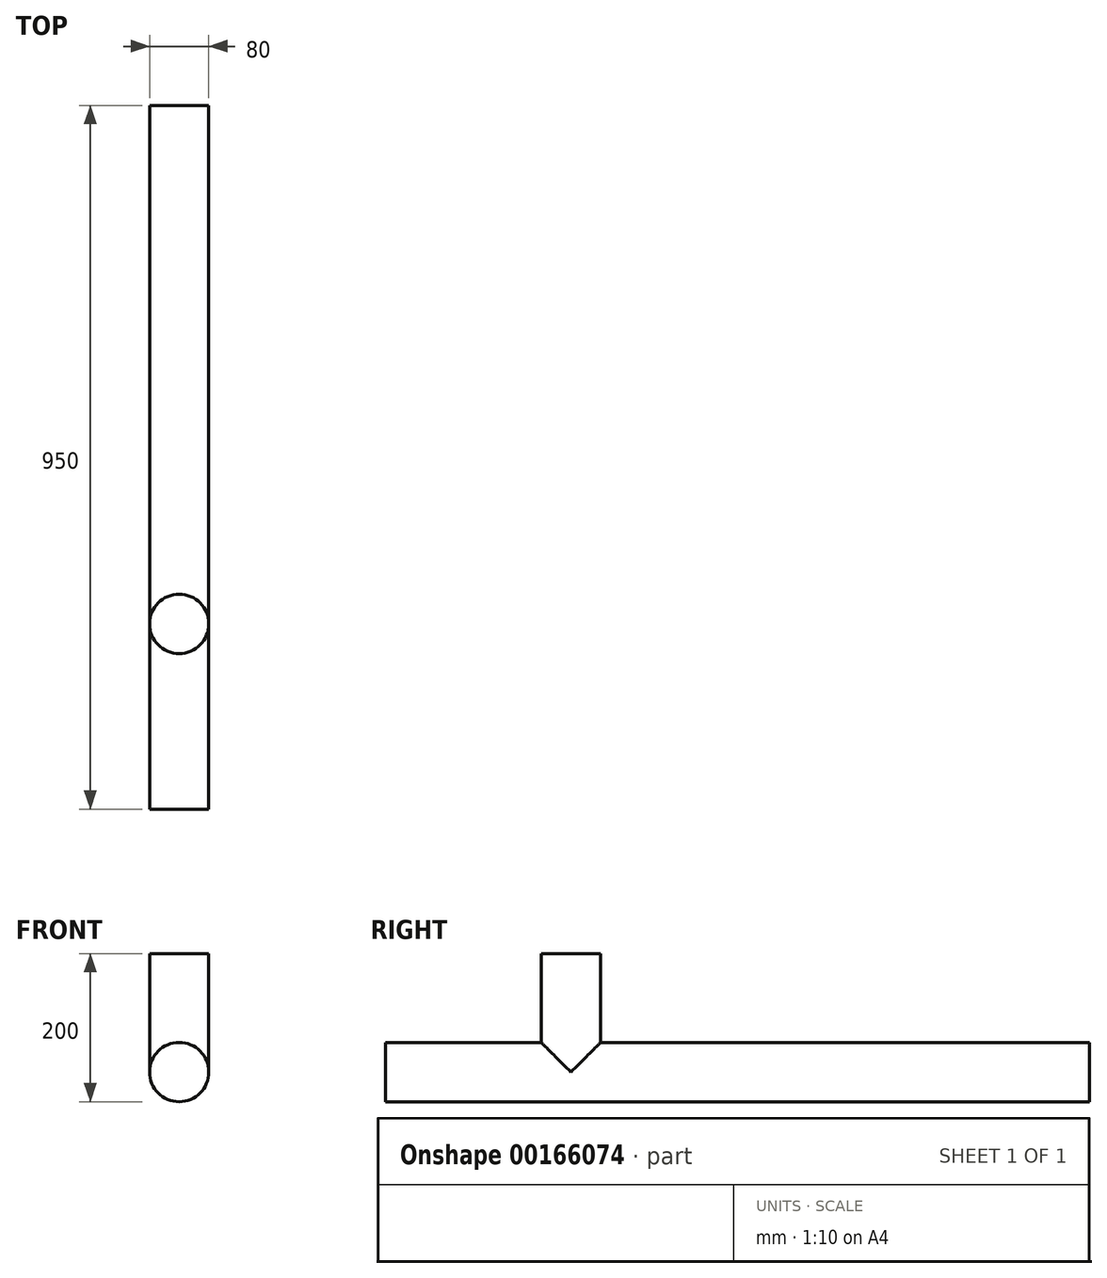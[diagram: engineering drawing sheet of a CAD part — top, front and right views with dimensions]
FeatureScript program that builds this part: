
annotation { "Feature Type Name" : "Feature", "Feature Type Description" : "" }
export const myFeature = defineFeature(function(context is Context, id is Id, definition is map)
    precondition{}
    {
        {
            var Q0;
            Q0=qCreatedBy(makeId("Front.planeOp"),FACE);
            var sketch = newSketch(context, id + "F0", { "sketchPlane" : qUnion([Q0])});
            skCircle(sketch, "E0", {"center": v(0, 0) * mm, "radius": 40 * mm});
            skSolve(sketch);
        }
        {
            var Q0;
            Q0 = qSketchRegion(id + "F0", true);
            extrude(context, id + "F1", {"entities" : qUnion([Q0]), "oppositeDirection" : true, "depth" : 700 * mm, "hasSecondDirection" : true, "secondDirectionOppositeDirection" : false, "secondDirectionDepth" : 250 * mm});
        }
        {
            var Q0;
            Q0=qCreatedBy(makeId("Top.planeOp"),FACE);
            var sketch = newSketch(context, id + "F2", { "sketchPlane" : qUnion([Q0])});
            skCircle(sketch, "E1", {"center": v(0, 0) * mm, "radius": 40 * mm});
            skSolve(sketch);
        }
        {
            var Q0;
            Q0 = qSketchRegion(id + "F2", true);
            extrude(context, id + "F3", {"entities" : qUnion([Q0]), "operationType" : NewBodyOperationType.ADD, "depth" : 160 * mm});
        }
    });
